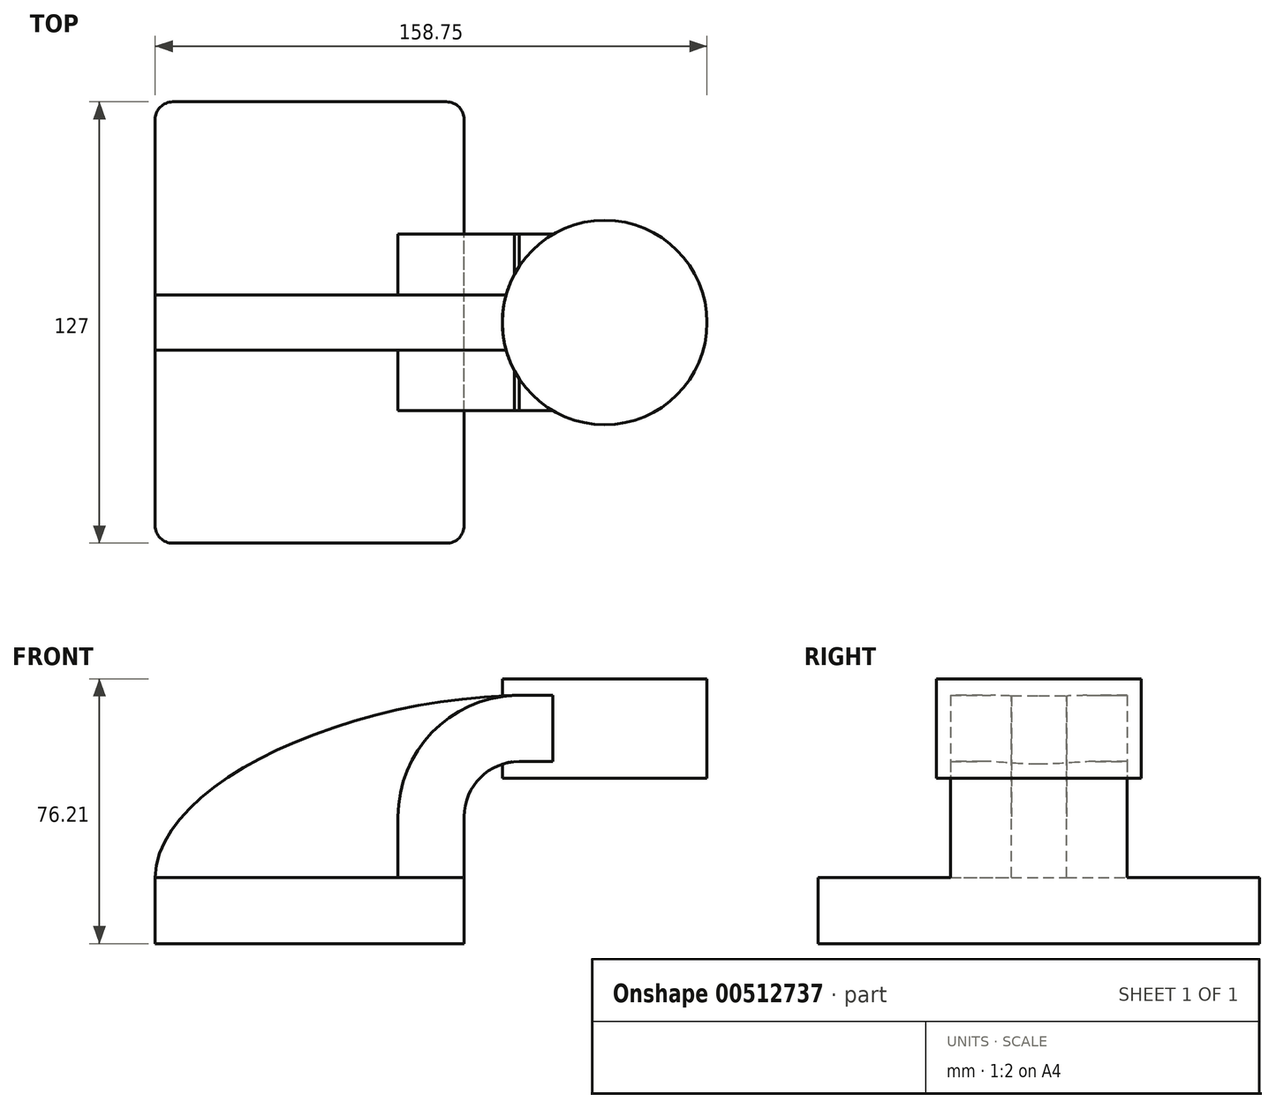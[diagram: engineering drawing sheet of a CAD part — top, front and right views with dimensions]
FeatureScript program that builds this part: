
annotation { "Feature Type Name" : "Feature", "Feature Type Description" : "" }
export const myFeature = defineFeature(function(context is Context, id is Id, definition is map)
    precondition{}
    {
        {
            var Q0;
            Q0=qCreatedBy(makeId("Front.planeOp"),FACE);
            var sketch = newSketch(context, id + "F0", { "sketchPlane" : qUnion([Q0])});
            skLineSegment(sketch, "E0.bottom", {"start": v(-44.45, 9.52) * mm, "end": v(44.45, 9.53) * mm});
            skLineSegment(sketch, "E0.top", {"start": v(-44.45, -9.53) * mm, "end": v(44.45, -9.53) * mm});
            skLineSegment(sketch, "E0.left", {"start": v(-44.45, 9.52) * mm, "end": v(-44.45, -9.53) * mm});
            skLineSegment(sketch, "E0.right", {"start": v(44.45, 9.53) * mm, "end": v(44.45, -9.52) * mm});
            skPoint(sketch, "E0.middle", {"position": v(0, 0) * mm});
            skLineSegment(sketch, "E1.bottom", {"start": v(63.5, 66.68) * mm, "end": v(114.3, 66.68) * mm});
            skLineSegment(sketch, "E1.top", {"start": v(63.5, 38.1) * mm, "end": v(114.3, 38.1) * mm});
            skLineSegment(sketch, "E1.left", {"start": v(63.5, 66.68) * mm, "end": v(63.5, 38.1) * mm});
            skLineSegment(sketch, "E1.right", {"start": v(114.3, 66.68) * mm, "end": v(114.3, 38.1) * mm});
            skPoint(sketch, "E1.middle", {"position": v(88.9, 52.39) * mm});
            skLineSegment(sketch, "E2", {"start": v(44.45, 9.53) * mm, "end": v(44.45, 27) * mm});
            skPoint(sketch, "E3.endSnap0", {"position": v(63.5, 52.39) * mm});
            skArc(sketch, "E4", {"start": v(44.45, 27) * mm, "mid": v(49.1, 38.23) * mm, "end": v(60.32, 42.88) * mm});
            skLineSegment(sketch, "E5", {"start": v(60.32, 42.88) * mm, "end": v(84.87, 42.88) * mm});
            skLineSegment(sketch, "E6.0", {"start": v(60.32, 61.93) * mm, "end": v(84.87, 61.93) * mm});
            skArc(sketch, "E6.1", {"start": v(25.4, 27) * mm, "mid": v(35.63, 51.7) * mm, "end": v(60.32, 61.93) * mm});
            skLineSegment(sketch, "E6.2", {"start": v(25.4, 9.53) * mm, "end": v(25.4, 27) * mm});
            skLineSegment(sketch, "E7", {"start": v(84.87, 38.1) * mm, "end": v(84.87, 66.68) * mm});
            skPoint(sketch, "E7.startSnap0", {"position": v(88.9, 38.1) * mm});
            skFitSpline(sketch, "E8", {"points": [v(-44.45, 9.52) * mm, v(60.32, 61.93) * mm], "startDerivative": vector(1.44, 82.04) * mm, "endDerivative": vector(148, 2.34) * mm});
            skSolve(sketch);
        }
        {
            var Q0;
            Q0=makeQuery(id+"F0.imprint","IMPRINT",FACE,{"disambiguationData":[TD([[makeQuery(id+"F0.imprint","IMPRINT",EDGE,{"derivedFrom":sQuery(id+"F0.wireOp",EDGE,"E0.top")}),1.0]])]});
            extrude(context, id + "F1", {"entities" : qUnion([Q0]), "endBound" : BoundingType.SYMMETRIC, "depth" : 127 * mm});
        }
        {
            var Q0;
            {var subQ1=sQuery(id+"F0.wireOp",EDGE,"E2");Q0=makeQuery(id+"F0.imprint","IMPRINT",FACE,{"disambiguationData":[TD([[makeQuery(id+"F0.imprint","IMPRINT",EDGE,{"derivedFrom":subQ1}),1.0]])]});}
            var Q1;
            {var subQ0=sQuery(id+"F0.wireOp",EDGE,"E6.0");var subQ1=sQuery(id+"F0.wireOp",EDGE,"E1.left");var subQ2=makeQuery(id+"F0.imprint","INTERSECT",VERTEX,{"derivedFrom":[subQ1,subQ0]});Q1=makeQuery(id+"F0.imprint","IMPRINT",FACE,{"disambiguationData":[TD([[makeQuery(id+"F0.imprint","IMPRINT",EDGE,{"disambiguationData":[TD([[subQ2,-1.0]])],"derivedFrom":subQ1}),1.0]])]});}
            extrude(context, id + "F2", {"entities" : qUnion([Q0, Q1]), "operationType" : NewBodyOperationType.ADD, "endBound" : BoundingType.SYMMETRIC, "depth" : 50.8 * mm});
        }
        {
            var Q0;
            {var subQ3=sQuery(id+"F0.wireOp",EDGE,"E6.2");Q0=makeQuery(id+"F0.imprint","IMPRINT",FACE,{"disambiguationData":[TD([[makeQuery(id+"F0.imprint","IMPRINT",EDGE,{"derivedFrom":subQ3}),1.0]])]});}
            extrude(context, id + "F3", {"entities" : qUnion([Q0]), "operationType" : NewBodyOperationType.ADD, "endBound" : BoundingType.SYMMETRIC, "depth" : 15.88 * mm});
        }
        {
            var Q0;
            {var subQ4=sQuery(id+"F0.wireOp",EDGE,"E1.right");Q0=makeQuery(id+"F0.imprint","IMPRINT",FACE,{"disambiguationData":[TD([[makeQuery(id+"F0.imprint","IMPRINT",EDGE,{"derivedFrom":subQ4}),-1.0]])]});}
            var Q1;
            Q1=sQuery(id+"F0.wireOp",EDGE,"E7");
            revolve(context, id + "F4", {"operationType" : NewBodyOperationType.ADD, "entities" : qUnion([Q0]), "axis" : qUnion([Q1]), "revolveType" : RevolveType.FULL});
        }
        {
            var Q0;
            Q0=makeQuery(id+"F1.opExtrude","CAP_EDGE",EDGE,{"disambiguationData":[OSD([sQuery(id+"F0.wireOp",EDGE,"E0.right")])],"isStart":false});
            var Q1;
            Q1=makeQuery(id+"F1.opExtrude","CAP_EDGE",EDGE,{"disambiguationData":[OSD([sQuery(id+"F0.wireOp",EDGE,"E0.left")])],"isStart":false});
            var Q2;
            Q2=makeQuery(id+"F1.opExtrude","CAP_EDGE",EDGE,{"disambiguationData":[OSD([sQuery(id+"F0.wireOp",EDGE,"E0.right")])],"isStart":true});
            var Q3;
            Q3=makeQuery(id+"F1.opExtrude","CAP_EDGE",EDGE,{"disambiguationData":[OSD([sQuery(id+"F0.wireOp",EDGE,"E0.left")])],"isStart":true});
            fillet(context, id + "F5", {"entities" : qUnion([Q0, Q1, Q2, Q3]), "radius" : 5.08 * mm, "tangentPropagation" : true, "allowEdgeOverflow" : false});
        }
    });
